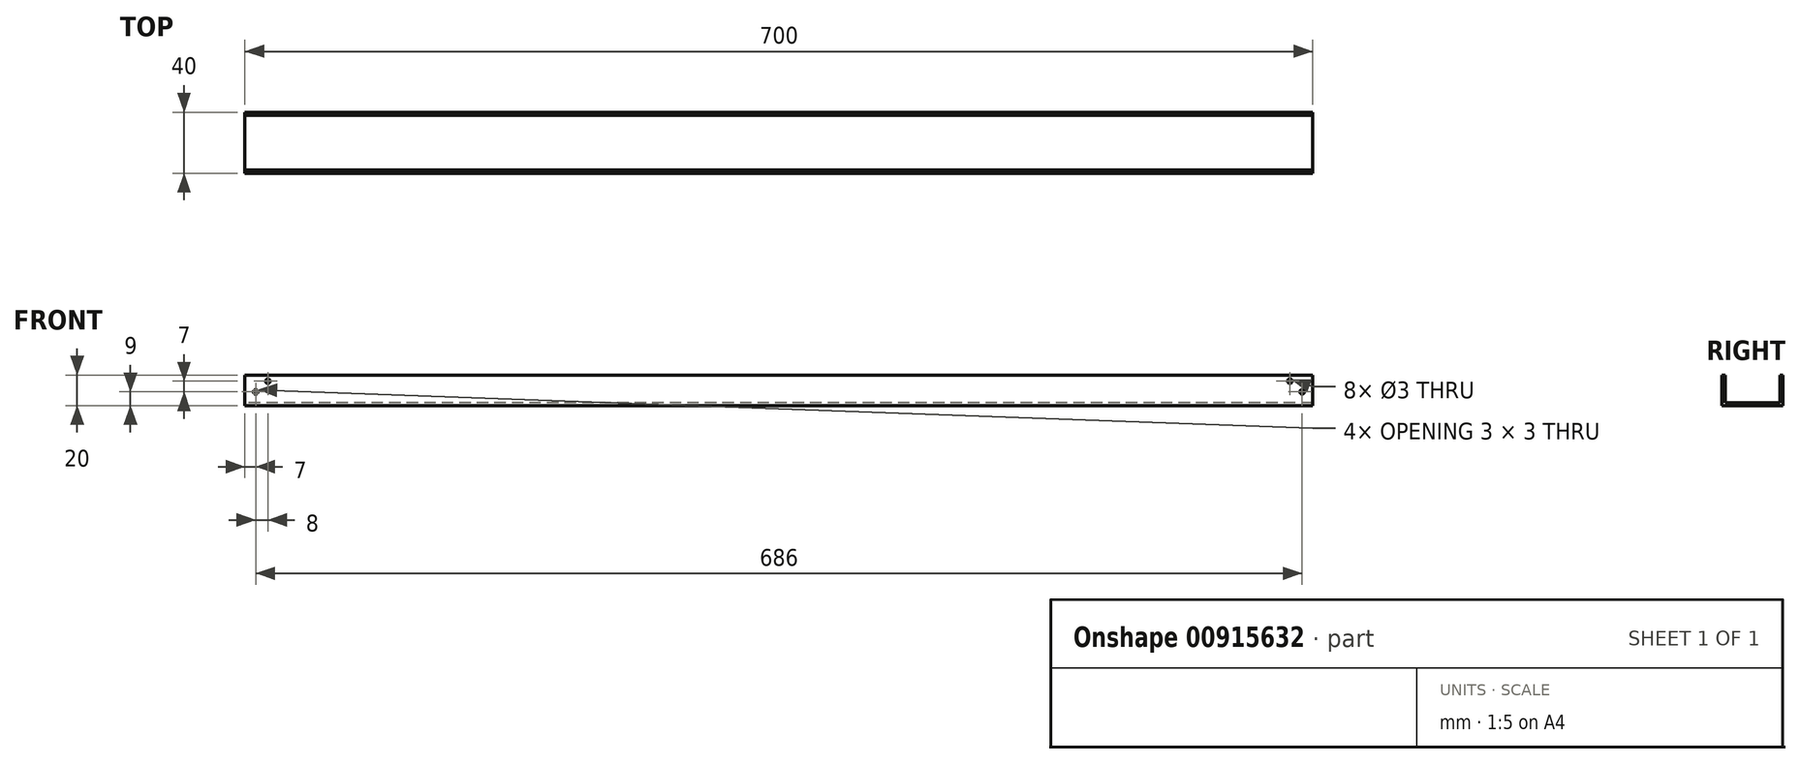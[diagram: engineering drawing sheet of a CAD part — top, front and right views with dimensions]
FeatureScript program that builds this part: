
annotation { "Feature Type Name" : "Feature", "Feature Type Description" : "" }
export const myFeature = defineFeature(function(context is Context, id is Id, definition is map)
    precondition{}
    {
        {
            var Q0;
            Q0=qCreatedBy(makeId("Right.planeOp"),FACE);
            var sketch = newSketch(context, id + "F0", { "sketchPlane" : qUnion([Q0])});
            skLineSegment(sketch, "E0.bottom", {"start": v(-20, 0) * mm, "end": v(20, 0) * mm});
            skLineSegment(sketch, "E0.top", {"start": v(-20, 20) * mm, "end": v(20, 20) * mm});
            skLineSegment(sketch, "E0.left", {"start": v(-20, 0) * mm, "end": v(-20, 20) * mm});
            skLineSegment(sketch, "E0.right", {"start": v(20, 0) * mm, "end": v(20, 20) * mm});
            skPoint(sketch, "E0.middle", {"position": v(0, 10) * mm});
            skLineSegment(sketch, "E1.bottom", {"start": v(-18, 20) * mm, "end": v(18, 20) * mm});
            skLineSegment(sketch, "E1.top", {"start": v(-18, 2) * mm, "end": v(18, 2) * mm});
            skLineSegment(sketch, "E1.left", {"start": v(-18, 20) * mm, "end": v(-18, 2) * mm});
            skLineSegment(sketch, "E1.right", {"start": v(18, 20) * mm, "end": v(18, 2) * mm});
            skPoint(sketch, "E1.middle", {"position": v(0, 11) * mm});
            skSolve(sketch);
        }
        {
            var Q0;
            Q0=makeQuery(id+"F0.imprint","IMPRINT",FACE,{"disambiguationData":[TD([[makeQuery(id+"F0.imprint","IMPRINT",EDGE,{"derivedFrom":sQuery(id+"F0.wireOp",EDGE,"E0.bottom")}),1.0]])]});
            extrude(context, id + "F1", {"entities" : qUnion([Q0]), "depth" : 350 * mm, "offsetDistance" : 25 * mm, "hasSecondDirection" : true, "secondDirectionOppositeDirection" : true, "secondDirectionDepth" : 350 * mm});
        }
        {
            var Q0;
            Q0=makeQuery(id+"F1.opExtrude","SWEPT_FACE",FACE,{"disambiguationData":[OSD([sQuery(id+"F0.wireOp",EDGE,"E1.left")])]});
            var sketch = newSketch(context, id + "F2", { "sketchPlane" : qUnion([Q0])});
            skLineSegment(sketch, "E2.bottom", {"start": v(350, 2) * mm, "end": v(343, 2) * mm});
            skLineSegment(sketch, "E2.top", {"start": v(350, 9) * mm, "end": v(343, 9) * mm});
            skLineSegment(sketch, "E2.left", {"start": v(350, 2) * mm, "end": v(350, 9) * mm});
            skLineSegment(sketch, "E2.right", {"start": v(343, 2) * mm, "end": v(343, 9) * mm});
            skLineSegment(sketch, "E3.bottom", {"start": v(-350, 2) * mm, "end": v(-343, 2) * mm});
            skLineSegment(sketch, "E3.top", {"start": v(-350, 9) * mm, "end": v(-343, 9) * mm});
            skLineSegment(sketch, "E3.left", {"start": v(-350, 2) * mm, "end": v(-350, 9) * mm});
            skLineSegment(sketch, "E3.right", {"start": v(-343, 2) * mm, "end": v(-343, 9) * mm});
            skLineSegment(sketch, "E4", {"start": v(343, 9) * mm, "end": v(343, 16) * mm});
            skLineSegment(sketch, "E5", {"start": v(335, 16) * mm, "end": v(343, 16) * mm});
            skLineSegment(sketch, "E6", {"start": v(-343, 9) * mm, "end": v(-343, 16) * mm});
            skLineSegment(sketch, "E7", {"start": v(-343, 16) * mm, "end": v(-335, 16) * mm});
            skSolve(sketch);
        }
        {
            var Q0;
            Q0=sQuery(id+"F2.wireOp",VERTEX,"E3.top.end");
            var Q1;
            Q1=sQuery(id+"F2.wireOp",VERTEX,"E2.top.end");
            var Q2;
            Q2=sQuery(id+"F2.wireOp",VERTEX,"E5.start");
            var Q3;
            Q3=sQuery(id+"F2.wireOp",VERTEX,"E7.end");
            var Q4;
            Q4=makeQuery(id+"F1.opExtrude","SWEPT_BODY",BODY,{"disambiguationData":[OSD([sQuery(id+"F0.wireOp",EDGE,"E0.bottom"),sQuery(id+"F0.wireOp",EDGE,"E0.top"),sQuery(id+"F0.wireOp",EDGE,"E0.left"),sQuery(id+"F0.wireOp",EDGE,"E0.right"),sQuery(id+"F0.wireOp",EDGE,"E1.top"),sQuery(id+"F0.wireOp",EDGE,"E1.left"),sQuery(id+"F0.wireOp",EDGE,"E1.right")])]});
            hole(context, id + "F3", {"style" : HoleStyle.SIMPLE, "endStyle" : HoleEndStyle.BLIND, "holeDiameter" : 3 * mm, "majorDiameter" : 5 * mm, "holeDepth" : 50 * mm, "isTappedThrough" : true, "tappedDepth" : 12 * mm, "tapClearance" : 3, "locations" : qUnion([Q0, Q1, Q2, Q3]), "scope" : qUnion([Q4])});
        }
        {
            var Q0;
            Q0=sQuery(id+"F2.wireOp",VERTEX,"E3.top.end");
            var Q1;
            Q1=sQuery(id+"F2.wireOp",VERTEX,"E2.top.end");
            var Q2;
            Q2=sQuery(id+"F2.wireOp",VERTEX,"E7.end");
            var Q3;
            Q3=sQuery(id+"F2.wireOp",VERTEX,"E5.start");
            var Q4;
            Q4=makeQuery(id+"F1.opExtrude","SWEPT_BODY",BODY,{"disambiguationData":[OSD([sQuery(id+"F0.wireOp",EDGE,"E0.bottom"),sQuery(id+"F0.wireOp",EDGE,"E0.top"),sQuery(id+"F0.wireOp",EDGE,"E0.left"),sQuery(id+"F0.wireOp",EDGE,"E0.right"),sQuery(id+"F0.wireOp",EDGE,"E1.top"),sQuery(id+"F0.wireOp",EDGE,"E1.left"),sQuery(id+"F0.wireOp",EDGE,"E1.right")])]});
            hole(context, id + "F4", {"style" : HoleStyle.SIMPLE, "endStyle" : HoleEndStyle.BLIND, "oppositeDirection" : true, "holeDiameter" : 3 * mm, "majorDiameter" : 5 * mm, "holeDepth" : 50 * mm, "isTappedThrough" : true, "tappedDepth" : 12 * mm, "tapClearance" : 3, "locations" : qUnion([Q0, Q1, Q2, Q3]), "scope" : qUnion([Q4])});
        }
    });
